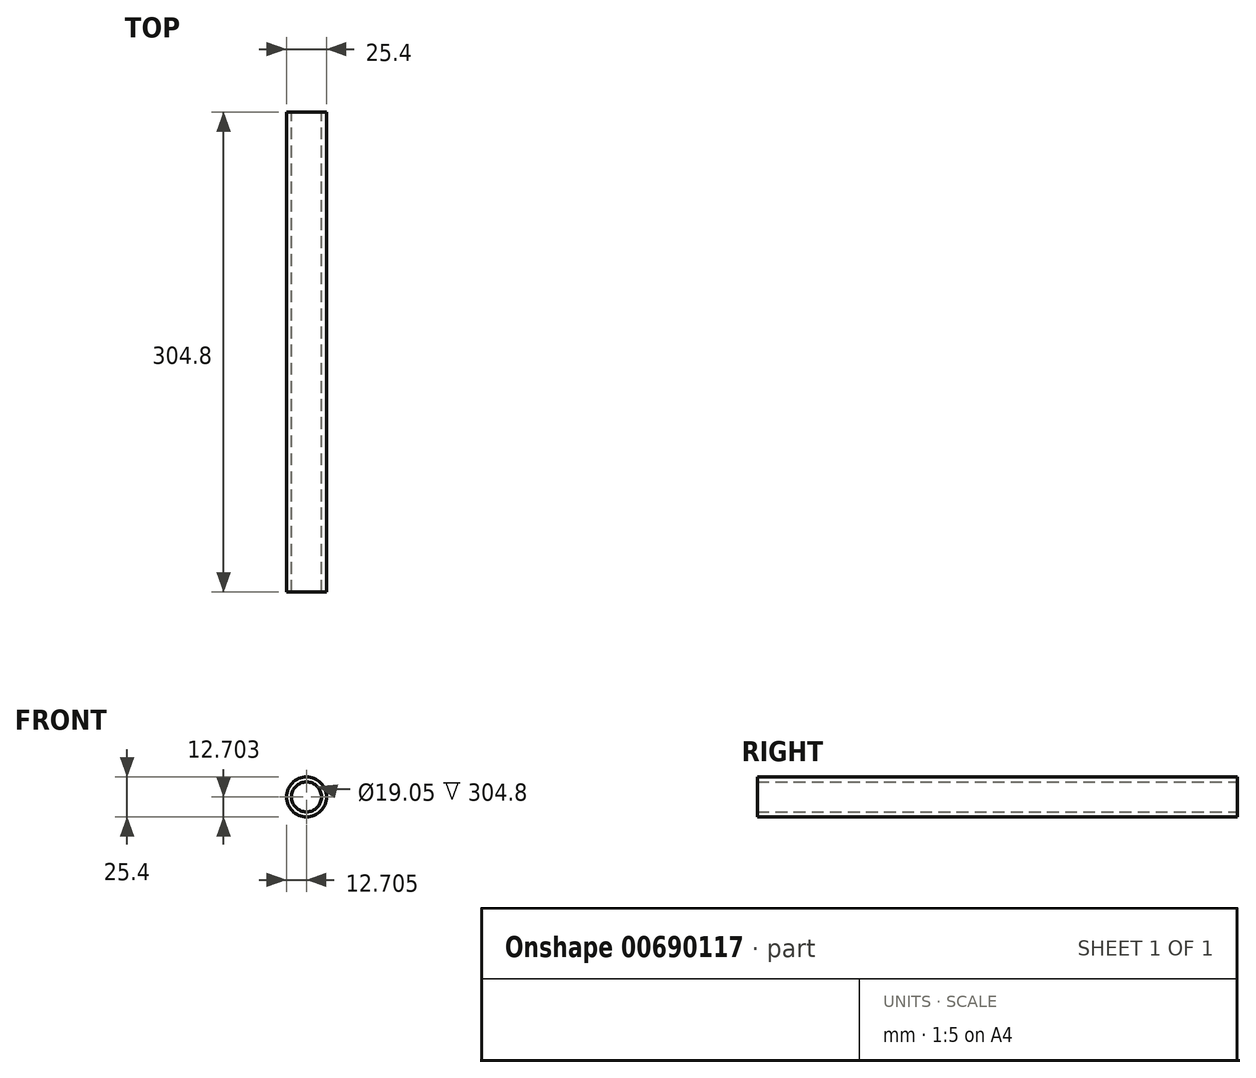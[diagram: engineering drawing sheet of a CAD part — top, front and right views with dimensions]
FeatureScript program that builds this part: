
annotation { "Feature Type Name" : "Feature", "Feature Type Description" : "" }
export const myFeature = defineFeature(function(context is Context, id is Id, definition is map)
    precondition{}
    {
        {
            var Q0;
            Q0=qCreatedBy(makeId("Front.planeOp"),FACE);
            var sketch = newSketch(context, id + "F0", { "sketchPlane" : qUnion([Q0])});
            skCircle(sketch, "E0", {"center": v(-15.75, -10.35) * mm, "radius": 12.7 * mm});
            skCircle(sketch, "E1", {"center": v(-15.75, -10.35) * mm, "radius": 9.53 * mm});
            skSolve(sketch);
        }
        {
            var Q0;
            Q0=makeQuery(id+"F0.imprint","IMPRINT",FACE,{"disambiguationData":[TD([[makeQuery(id+"F0.imprint","IMPRINT",EDGE,{"derivedFrom":sQuery(id+"F0.wireOp",EDGE,"E0")}),1.0]])]});
            extrude(context, id + "F1", {"entities" : qUnion([Q0]), "depth" : 304.8 * mm, "offsetDistance" : 25.4 * mm});
        }
    });
